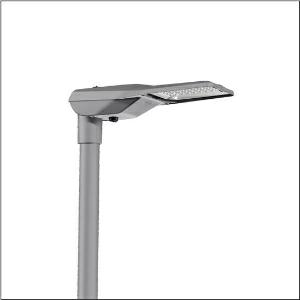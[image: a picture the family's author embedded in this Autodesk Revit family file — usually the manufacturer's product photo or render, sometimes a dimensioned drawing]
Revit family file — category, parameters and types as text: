
# Revit family: streetlight_sl_21_iq_mini___st1_0a_5xe2d61y08gb_62ef
name_source: partatom
category: Lighting Fixtures
units: mm (PartAtom-declared; Revit-internal decimal feet)

## family parameters
Cut with Voids When Loaded = No
Host = Face
Light Source = No
Part Type = Normal
Room Calculation Point = No
Round Connector Dimension = Use Diameter
Shared = No

## types (1)
- --- (1 x LED, 5200 lm, 39.8 W, 2700K)
    Apparent Load = 40 VA
    CIE Flux Codes = 37 72 97 100 100
    Color Rendering = 70
    Color Temperature = 2700K
    Default Elevation = 1800 mm
    Description = Streetlight SL 21 iQ mini, mast luminaire, primary light control with lens, of PMMA, primary optical cover: cover, of toughened safety glass, transparent, light distribution: ST1.0a, light emission: direct distribution, primary light characteristic: asymmetric, installation type: post-top, side-entry, LED, High Power LED, rated luminous flux: 5.200lm, luminous efficacy: 131lm/W, light colour: 727, colour temperature: 2700K, control: presetting dimming logarithmic, Street-Remote, Auto-Match, Temp-Guard, Lumen-Switch, Night-Set, Smart-Wire, Light-Fading, Desk-Remote (wireless, voltage-free reading and setting of iQ features in the workshop via application-optimized NFC function/RFID function), optimised constant luminous flux control (CLO 2.0), mains connection: 220..240V, AC, 50/60Hz, start of lifetime: 40W, end of service life: 41W, reduction: 18W, luminaire housing, of diecast aluminium, powder-coated, Siteco® metallic grey (DB 702S), corrosivity category C5 mid according to DIN EN ISO 12944, please order mast flange separately, inclination adjustable: 0°, 5°, 10°, 15°, sealing non-destructively replaceable, multi-level sealing system, length: 628mm, width: 235mm, height: 110mm, mast flange for spigot size: 42mm (side-entry): 5XC10008XM4, 60/48mm (side-entry/post-top): 5XC10108XM2, 76/60mm (side-entry/post-top): 5XC10108XM1, Smart Interface below and above, protection rating (complete): IP66, insulation class (complete): insulation class II (safety insulation), certification: CE, ENEC, ENEC+, VDE, impact resistance: IK09, permissible operating ambient temperature for outdoor applications: -40..+50°C, standard-compliant lighting for roads and squares, packaging unit: 1 piece

Light Distribution: ST1.0a
    Height = 110 mm
    Lamp = 1 x LED
    Lamp Light Flux = 5200 lm
    Lamp Power = 39.8 W
    Lamp count = 1
    Length = 625 mm
    Luminous efficacy = 131 lm/W
    Manufacturer = Siteco
    ModVariant = No
    Model = 5XE2D61Y08GB
    Number of Poles = 1
    OnlyDefault = Yes
    Power Factor = 1
    Product Name = Streetlight SL 21 iQ mini | ST1.0a
    Product group = mast luminaire | pylon top
    ProductGroupID = 6100
    Protection Class = Protection class II
    Protection Degree = IP 66
    RLX_Detail_Level = 1
    RLX_Emergency_Light_Flux = 0 lm
    RLX_Emergency_Type = 0
    RLX_Emergency_Type_DB = No
    RlxData = <blob elided: 92397 chars, md5=2ae65199>
    Socket = socket
    Standby Power = 0 W
    System Light Flux = 5200 lm
    System Power = 40 W
    Type Comments = factory setting: luminous flux: 100 % | dim-lin: 254 | 800 mA
    Type Image = l_1003514.jpg
    URL = http://relux.com
    VarID = @adj_045031
    Voltage = 0 V
    Weight = 0.00 kg
    Width = 234 mm

## geometry (parser evidence)
native form markers: Blend x4, Sweep x10
no freeform markers — native parametric forms only
